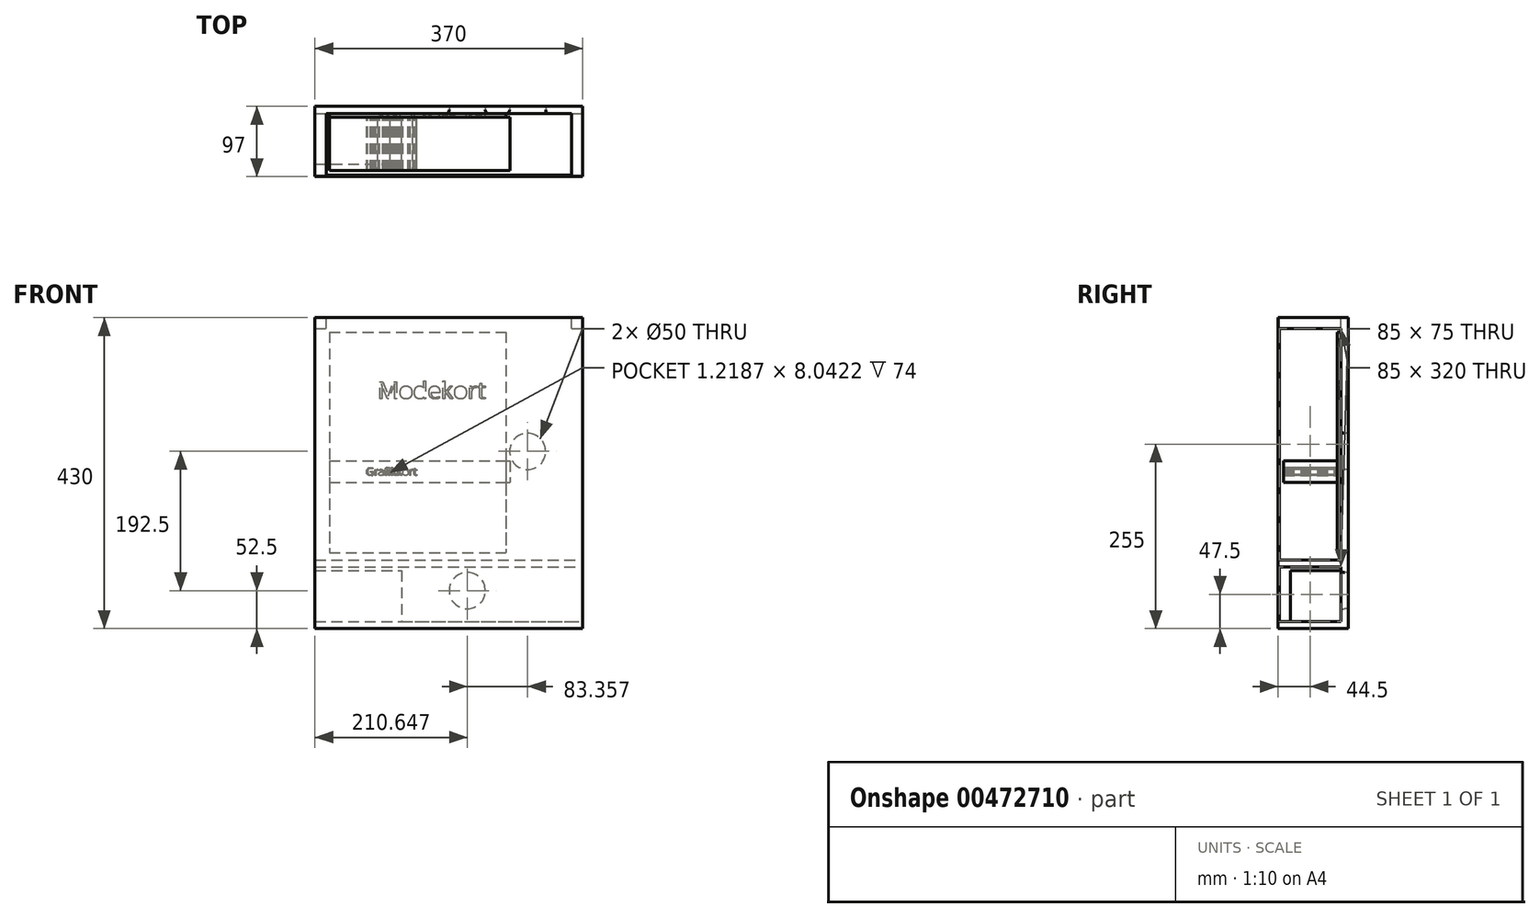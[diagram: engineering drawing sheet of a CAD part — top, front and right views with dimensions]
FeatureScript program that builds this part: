
annotation { "Feature Type Name" : "Feature", "Feature Type Description" : "" }
export const myFeature = defineFeature(function(context is Context, id is Id, definition is map)
    precondition{}
    {
        {
            var Q0;
            Q0=qCreatedBy(makeId("Front.planeOp"),FACE);
            var sketch = newSketch(context, id + "F0", { "sketchPlane" : qUnion([Q0])});
            skLineSegment(sketch, "E0.bottom", {"start": v(-40.73, 272.17) * mm, "end": v(203.27, 272.17) * mm});
            skLineSegment(sketch, "E0.top", {"start": v(-40.73, -32.83) * mm, "end": v(203.27, -32.83) * mm});
            skLineSegment(sketch, "E0.left", {"start": v(-40.73, 272.17) * mm, "end": v(-40.73, -32.83) * mm});
            skLineSegment(sketch, "E0.right", {"start": v(203.27, 272.17) * mm, "end": v(203.27, -32.83) * mm});
            skText(sketch, "E1", { "text": "Modekort", "fontName": "OpenSans-Regular.ttf"});
            const initialGuessF0  = {"E1": [0.0259, 0.17988, 1, 0, 0.02354]};
            skSetInitialGuess(sketch, initialGuessF0);
            skSolve(sketch);
        }
        {
            var Q0;
            Q0=makeQuery(id+"F0.imprint","IMPRINT",FACE,{"disambiguationData":[TD([[makeQuery(id+"F0.imprint","IMPRINT",EDGE,{"derivedFrom":sQuery(id+"F0.wireOp",EDGE,"E0.bottom")}),-1.0]])]});
            extrude(context, id + "F1", {"entities" : qUnion([Q0]), "depth" : 5 * mm});
        }
        {
            var Q0;
            Q0=qCreatedBy(makeId("Front.planeOp"),FACE);
            var sketch = newSketch(context, id + "F2", { "sketchPlane" : qUnion([Q0])});
            skLineSegment(sketch, "E2.bottom", {"start": v(-60.73, -137.83) * mm, "end": v(309.27, -137.83) * mm});
            skLineSegment(sketch, "E2.top", {"start": v(-60.73, 292.17) * mm, "end": v(309.27, 292.17) * mm});
            skLineSegment(sketch, "E2.left", {"start": v(-60.73, -137.83) * mm, "end": v(-60.73, 292.17) * mm});
            skLineSegment(sketch, "E2.right", {"start": v(309.27, -137.83) * mm, "end": v(309.27, 292.17) * mm});
            skSolve(sketch);
        }
        {
            var Q0;
            Q0=qCreatedBy(makeId("Front.planeOp"),FACE);
            var sketch = newSketch(context, id + "F3", { "sketchPlane" : qUnion([Q0])});
            skCircle(sketch, "E3", {"center": v(233.27, 107.17) * mm, "radius": 25 * mm});
            skSolve(sketch);
        }
        {
            var Q0;
            Q0 = qSketchRegion(id + "F2", true);
            extrude(context, id + "F4", {"entities" : qUnion([Q0]), "operationType" : NewBodyOperationType.ADD, "oppositeDirection" : true, "depth" : 10 * mm});
        }
        {
            var Q0;
            Q0 = qSketchRegion(id + "F3", true);
            extrude(context, id + "F5", {"entities" : qUnion([Q0]), "operationType" : NewBodyOperationType.REMOVE, "endBound" : BoundingType.SYMMETRIC, "oppositeDirection" : true, "depth" : 25 * mm});
        }
        {
            var Q0;
            Q0=qCreatedBy(makeId("Front.planeOp"),FACE);
            var sketch = newSketch(context, id + "F6", { "sketchPlane" : qUnion([Q0])});
            skLineSegment(sketch, "E4.bottom", {"start": v(-60.73, -42.83) * mm, "end": v(309.27, -42.83) * mm});
            skLineSegment(sketch, "E4.top", {"start": v(-60.73, -52.83) * mm, "end": v(309.27, -52.83) * mm});
            skLineSegment(sketch, "E4.left", {"start": v(-60.73, -42.83) * mm, "end": v(-60.73, -52.83) * mm});
            skLineSegment(sketch, "E4.right", {"start": v(309.27, -52.83) * mm, "end": v(309.27, -42.83) * mm});
            skSolve(sketch);
        }
        {
            var Q0;
            Q0 = qSketchRegion(id + "F6", true);
            extrude(context, id + "F7", {"entities" : qUnion([Q0]), "operationType" : NewBodyOperationType.ADD, "depth" : 85 * mm});
        }
        {
            var Q0;
            Q0=qCreatedBy(makeId("Front.planeOp"),FACE);
            var sketch = newSketch(context, id + "F8", { "sketchPlane" : qUnion([Q0])});
            skLineSegment(sketch, "E5.bottom", {"start": v(-60.73, -137.83) * mm, "end": v(309.27, -137.83) * mm});
            skLineSegment(sketch, "E5.top", {"start": v(-60.73, -127.83) * mm, "end": v(309.27, -127.83) * mm});
            skLineSegment(sketch, "E5.left", {"start": v(-60.73, -127.83) * mm, "end": v(-60.73, -137.83) * mm});
            skLineSegment(sketch, "E5.right", {"start": v(309.27, -137.83) * mm, "end": v(309.27, -127.83) * mm});
            skSolve(sketch);
        }
        {
            var Q0;
            Q0 = qSketchRegion(id + "F8", true);
            extrude(context, id + "F9", {"entities" : qUnion([Q0]), "operationType" : NewBodyOperationType.ADD, "depth" : 85 * mm});
        }
        {
            var Q0;
            Q0=qCreatedBy(makeId("Front.planeOp"),FACE);
            var sketch = newSketch(context, id + "F10", { "sketchPlane" : qUnion([Q0])});
            skCircle(sketch, "E6", {"center": v(149.92, -85.33) * mm, "radius": 25 * mm});
            skSolve(sketch);
        }
        {
            var Q0;
            Q0=makeQuery(id+"F10.imprint","IMPRINT",FACE,{"disambiguationData":[TD([[makeQuery(id+"F10.imprint","IMPRINT",EDGE,{"derivedFrom":sQuery(id+"F10.wireOp",EDGE,"E6")}),1.0]])]});
            extrude(context, id + "F11", {"entities" : qUnion([Q0]), "operationType" : NewBodyOperationType.REMOVE, "endBound" : BoundingType.SYMMETRIC, "oppositeDirection" : true, "depth" : 25 * mm});
        }
        {
            var Q0;
            Q0=qCreatedBy(makeId("Front.planeOp"),FACE);
            var sketch = newSketch(context, id + "F12", { "sketchPlane" : qUnion([Q0])});
            skLineSegment(sketch, "E7.bottom", {"start": v(294.27, 277.17) * mm, "end": v(309.27, 277.17) * mm});
            skLineSegment(sketch, "E7.top", {"start": v(294.27, 292.17) * mm, "end": v(309.27, 292.17) * mm});
            skLineSegment(sketch, "E7.left", {"start": v(294.27, 277.17) * mm, "end": v(294.27, 292.17) * mm});
            skLineSegment(sketch, "E7.right", {"start": v(309.27, 277.17) * mm, "end": v(309.27, 292.17) * mm});
            skLineSegment(sketch, "E8.bottom", {"start": v(-60.73, 277.17) * mm, "end": v(-44.73, 277.17) * mm});
            skLineSegment(sketch, "E8.top", {"start": v(-60.73, 292.17) * mm, "end": v(-44.73, 292.17) * mm});
            skLineSegment(sketch, "E8.left", {"start": v(-60.73, 277.17) * mm, "end": v(-60.73, 292.17) * mm});
            skLineSegment(sketch, "E8.right", {"start": v(-44.73, 277.17) * mm, "end": v(-44.73, 292.17) * mm});
            skSolve(sketch);
        }
        {
            var Q0;
            Q0=makeQuery(id+"F5.boolean.opBoolean","INTERSECT",EDGE,{"derivedFrom":[makeQuery(id+"F4.opExtrude","CAP_FACE",FACE,{"disambiguationData":[OSD([sQuery(id+"F2.wireOp",EDGE,"E2.bottom"),sQuery(id+"F2.wireOp",EDGE,"E2.top"),sQuery(id+"F2.wireOp",EDGE,"E2.left"),sQuery(id+"F2.wireOp",EDGE,"E2.right")])],"isStart":true}),makeQuery(id+"F5.opExtrude","SWEPT_FACE",FACE,{"disambiguationData":[OSD([sQuery(id+"F3.wireOp",EDGE,"E3")])]})]});
            var Q1;
            {var subQ0=sQuery(id+"F2.wireOp",EDGE,"E2.right");var subQ1=sQuery(id+"F2.wireOp",EDGE,"E2.left");var subQ2=sQuery(id+"F2.wireOp",EDGE,"E2.bottom");Q1=makeQuery(id+"F11.boolean.opBoolean","INTERSECT",EDGE,{"derivedFrom":[makeQuery(id+"F7.boolean.opBoolean","SPLIT",FACE,{"disambiguationData":[TD([makeQuery(id+"F4.opExtrude","SWEPT_FACE",FACE,{"disambiguationData":[OSD([subQ2])]})])],"derivedFrom":makeQuery(id+"F4.opExtrude","CAP_FACE",FACE,{"disambiguationData":[OSD([subQ2,sQuery(id+"F2.wireOp",EDGE,"E2.top"),subQ1,subQ0])],"isStart":true})}),makeQuery(id+"F11.opExtrude","SWEPT_FACE",FACE,{"disambiguationData":[OSD([sQuery(id+"F10.wireOp",EDGE,"E6")])]})]});}
            fillet(context, id + "F13", {"entities" : qUnion([Q0, Q1]), "radius" : 5 * mm, "tangentPropagation" : true, "allowEdgeOverflow" : false});
        }
        {
            var Q0;
            Q0 = qSketchRegion(id + "F12", true);
            extrude(context, id + "F14", {"entities" : qUnion([Q0]), "operationType" : NewBodyOperationType.ADD, "depth" : 85 * mm});
        }
        {
            var Q0;
            Q0=makeQuery(id+"F1.opExtrude","CAP_FACE",FACE,{"disambiguationData":[OSD([sQuery(id+"F0.wireOp",EDGE,"E0.bottom"),sQuery(id+"F0.wireOp",EDGE,"E0.top"),sQuery(id+"F0.wireOp",EDGE,"E0.left"),sQuery(id+"F0.wireOp",EDGE,"E0.right")])],"isStart":false});
            var sketch = newSketch(context, id + "F15", { "sketchPlane" : qUnion([Q0])});
            skLineSegment(sketch, "E9.bottom", {"start": v(-40.73, 94.08) * mm, "end": v(209.27, 94.08) * mm});
            skLineSegment(sketch, "E9.top", {"start": v(-40.73, 64.08) * mm, "end": v(209.27, 64.08) * mm});
            skLineSegment(sketch, "E9.left", {"start": v(-40.73, 94.08) * mm, "end": v(-40.73, 64.08) * mm});
            skLineSegment(sketch, "E9.right", {"start": v(209.27, 94.08) * mm, "end": v(209.27, 64.08) * mm});
            skText(sketch, "E10", { "text": "Grafikkort\n", "fontName": "OpenSans-Regular.ttf"});
            const initialGuessF15  = {"E10": [0.00984, 0.07388, 1, 0, 0.01082]};
            skSetInitialGuess(sketch, initialGuessF15);
            skSolve(sketch);
        }
        {
            var Q0;
            Q0 = qSketchRegion(id + "F15", true);
            extrude(context, id + "F16", {"entities" : qUnion([Q0]), "operationType" : NewBodyOperationType.ADD, "depth" : 74 * mm});
        }
        {
            var Q0;
            Q0=qCreatedBy(makeId("Front.planeOp"),FACE);
            var sketch = newSketch(context, id + "F17", { "sketchPlane" : qUnion([Q0])});
            skLineSegment(sketch, "E11.bottom", {"start": v(-60.73, -57.83) * mm, "end": v(59.27, -57.83) * mm});
            skLineSegment(sketch, "E11.top", {"start": v(-60.73, -127.83) * mm, "end": v(59.27, -127.83) * mm});
            skLineSegment(sketch, "E11.left", {"start": v(-60.73, -57.83) * mm, "end": v(-60.73, -127.83) * mm});
            skLineSegment(sketch, "E11.right", {"start": v(59.27, -57.83) * mm, "end": v(59.27, -127.83) * mm});
            skSolve(sketch);
        }
        {
            var Q0;
            Q0 = qSketchRegion(id + "F17", true);
            extrude(context, id + "F18", {"entities" : qUnion([Q0]), "operationType" : NewBodyOperationType.ADD, "depth" : 70 * mm});
        }
        {
            var Q0;
            Q0=makeQuery(id+"F14.opExtrude","CAP_FACE",FACE,{"disambiguationData":[OSD([sQuery(id+"F12.wireOp",EDGE,"E8.bottom"),sQuery(id+"F12.wireOp",EDGE,"E8.top"),sQuery(id+"F12.wireOp",EDGE,"E8.left"),sQuery(id+"F12.wireOp",EDGE,"E8.right")])],"isStart":false});
            var sketch = newSketch(context, id + "F19", { "sketchPlane" : qUnion([Q0])});
            skLineSegment(sketch, "E12.bottom", {"start": v(-60.73, 292.17) * mm, "end": v(309.27, 292.17) * mm});
            skLineSegment(sketch, "E12.top", {"start": v(-60.73, -137.83) * mm, "end": v(309.27, -137.83) * mm});
            skLineSegment(sketch, "E12.left", {"start": v(-60.73, 292.17) * mm, "end": v(-60.73, -137.83) * mm});
            skLineSegment(sketch, "E12.right", {"start": v(309.27, 292.17) * mm, "end": v(309.27, -137.83) * mm});
            skSolve(sketch);
        }
        {
            var Q0;
            Q0 = qSketchRegion(id + "F19", true);
            extrude(context, id + "F20", {"entities" : qUnion([Q0]), "operationType" : NewBodyOperationType.ADD, "depth" : 2 * mm});
        }
    });
